# Revit family: LBSD
name_source: partatom
category: Lighting Fixtures
units: mm (PartAtom-declared; Revit-internal decimal feet)

## family parameters
Cut with Voids When Loaded = No
Host = Face
Light Source = Yes
OmniClass Number = 23.80.70.11
OmniClass Title = Luminaries for Internal Lighting
Part Type = Normal
Room Calculation Point = No
Round Connector Dimension = Use Diameter
Shared = No

## types (2) — shared parameters
Apparent Load = 0 VA
Backbox = White
CRI = 90+ CRI
Certifications = cETLus listed to UL1598
• Can be used in direct contact with insulation
(IC Rated)
• Suitable for wet locations, covered ceiling
• Suitable for use in clothes closets when
installed in accordance to N.E.C. 410.16
• ENERGY STAR® certified
• Meets CA Title 24 High Efficacy (JA8-2019)
requirements
Color Filter = 16777215
Default Elevation = 48 "
Description = Designed for use in new construction or retrofit IC or Non-IC applications
Dimming Lamp Color Temperature Shift = <None>
Features = 4inch and 6inch disk downlight delivering 700 or 1000 lumens 
Switchable CCT – 2700K/3000K/3500K/4000K 
90 CRI 
Universal Voltage (120-277V) 
Phase Dimmable to 5% (120V Triac/ELV) 
Surface mount directly to standard J-Box (by others) 
Optional accessory for retrofit into incandescent recessed cans
Glass = White Glass
Lamp = LED Lamp
Manufacturer = Prescolite Lighting
Model = LBSD-RD
Tilt Angle = -90.00°
URL = https://www.currentlighting.com
Voltage = 120 V
Wattage Comments = 11.5W
Watts = 17 W

## per-type parameters (varying)
| type | Inner Width | Photometric Web File | Width |
| LBSD-4RD | 2 " | LBSD-4RD-CS9-WH _27K.IES | 5.51 " |
| LBSD-6RD | 2.75 " | LBSD-6RD-CS9-WH_27K.IES | 7.32 " |

## geometry (parser evidence)
native form markers: Sweep x2
no freeform markers — native parametric forms only
